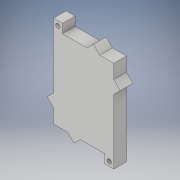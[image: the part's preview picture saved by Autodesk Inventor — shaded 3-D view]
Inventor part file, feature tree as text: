
AUTODESK INVENTOR PART (.ipt)
format: ipt  version: 2019 (Build 230136000, 136)  size: 205,312 bytes
history: native  units: mm
features: extrude x8, sketch x7
ambient origin geometry x8: Origin, YZ Plane, XZ Plane, XY Plane, X Axis, Y Axis, Z Axis, Center Point
bodies: Volumenkörper1 (feature_tree)
feature tree (15):
  sketch  "Skizze1"  dims[d0=50.5mm d1=35.5mm]
  extrude  "Extrusion1"  Depth=35.5mm
  extrude  "Extrusion2"  Depth=2.5mm TaperAngle=0.0deg
  extrude  "Extrusion3"  Depth=6.0mm
  extrude  "Extrusion4"  Depth=6.0mm
  extrude  "Extrusion5"  Depth=6.0mm TaperAngle=0.0deg
  extrude  "Extrusion8"  Depth=7.0mm
  extrude  "Extrusion9"  Depth=10.0mm
  extrude  "Extrusion12"  Depth=2.5mm TaperAngle=0.0deg
  sketch  "Skizze2"  dims[d2=2.5mm d3=2.5mm d4=0.0mm]
  sketch  "Skizze3"  dims[d5=6.0mm d6=0.0mm d7=3.0mm]
  sketch  "Skizze4"  dims[d8=77.5mm d9=0.0mm d11=6.0mm]
  sketch  "Skizze7"  dims[d12=6.0mm d13=0.0mm d15=6.0mm d16=0.0mm]
  sketch  "Skizze8"  dims[d26=7.0mm d27=7.0mm]
  sketch  "Skizze11"  dims[d28=3.3mm d29=3.3mm d30=2.5mm d31=0.0mm d32=2.5mm d33=0.0mm d42=6.0mm d43=3.0mm d44=10.0mm d45=0.0mm]
